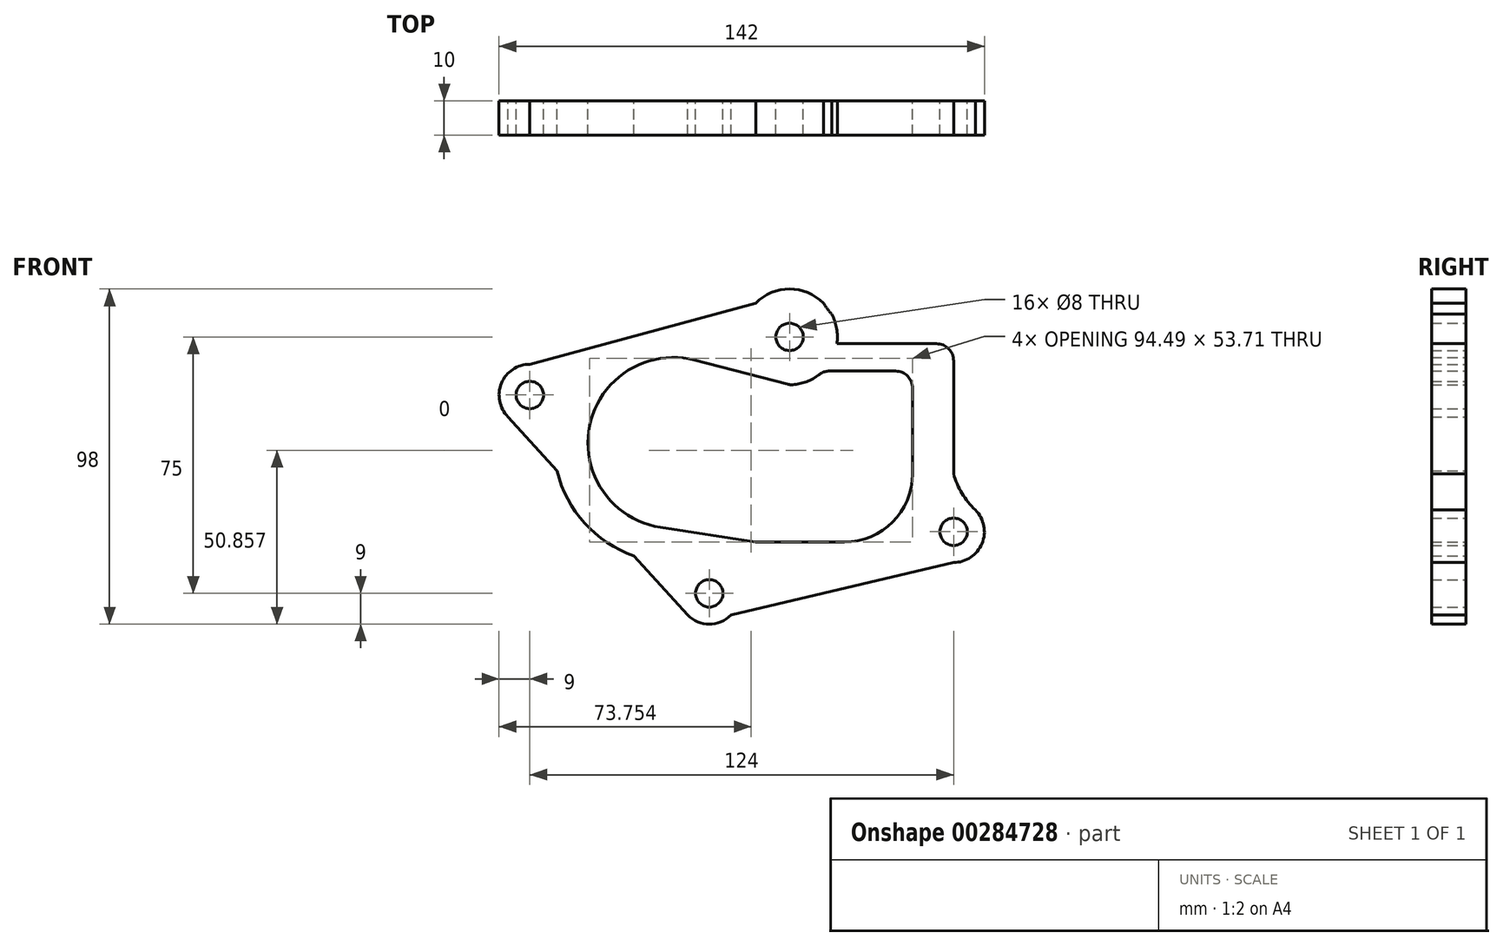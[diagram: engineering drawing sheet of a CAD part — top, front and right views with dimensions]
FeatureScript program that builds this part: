
annotation { "Feature Type Name" : "Feature", "Feature Type Description" : "" }
export const myFeature = defineFeature(function(context is Context, id is Id, definition is map)
    precondition{}
    {
        {
            var Q0;
            Q0=qCreatedBy(makeId("Front.planeOp"),FACE);
            var sketch = newSketch(context, id + "F0", { "sketchPlane" : qUnion([Q0])});
            skCircle(sketch, "E0", {"center": v(0, 0) * mm, "radius": 25 * mm});
            skLineSegment(sketch, "E1", {"start": v(0, 0) * mm, "end": v(70, 0) * mm});
            skPoint(sketch, "E2", {"position": v(34, 31) * mm});
            skArc(sketch, "E3", {"start": v(34.89, 17.03) * mm, "mid": v(38.96, 17.9) * mm, "end": v(42.6, 19.95) * mm, "construction": true});
            skLineSegment(sketch, "E4", {"start": v(34, 31) * mm, "end": v(34, 17) * mm, "construction": true});
            skPoint(sketch, "E5", {"position": v(0, 25) * mm});
            skLineSegment(sketch, "E6", {"start": v(33.31, 17.18) * mm, "end": v(6.28, 24.2) * mm});
            skLineSegment(sketch, "E7", {"start": v(70, 0) * mm, "end": v(70, -9) * mm});
            skLineSegment(sketch, "E8", {"start": v(50, -29) * mm, "end": v(24, -29) * mm});
            skPoint(sketch, "E9.visualSharp", {"position": v(70, -29) * mm});
            skArc(sketch, "E9.filletArc", {"start": v(50, -29) * mm, "mid": v(64.14, -23.14) * mm, "end": v(70, -9) * mm});
            skPoint(sketch, "E10.visualSharp", {"position": v(34, 17) * mm});
            skArc(sketch, "E10.filletArc", {"start": v(33.31, 17.18) * mm, "mid": v(34.1, 17.04) * mm, "end": v(34.89, 17.03) * mm});
            skLineSegment(sketch, "E11", {"start": v(24, -29) * mm, "end": v(-3.81, -24.7) * mm});
            skPoint(sketch, "E12", {"position": v(25, 0) * mm});
            skCircle(sketch, "E13", {"center": v(0, 0) * mm, "radius": 35 * mm, "construction": true});
            skPoint(sketch, "E14", {"position": v(-42, 14) * mm});
            skPoint(sketch, "E15", {"position": v(10.5, -44) * mm});
            skPoint(sketch, "E16", {"position": v(82, -26) * mm});
            skLineSegment(sketch, "E17", {"start": v(65.66, 21) * mm, "end": v(43.8, 21) * mm});
            skArc(sketch, "E18", {"start": v(43.8, 21) * mm, "mid": v(39.7, 18.21) * mm, "end": v(34.89, 17.03) * mm});
            skCircle(sketch, "E19", {"center": v(-42, 14) * mm, "radius": 4 * mm});
            skCircle(sketch, "E20", {"center": v(10.5, -44) * mm, "radius": 4 * mm});
            skCircle(sketch, "E21", {"center": v(82, -26) * mm, "radius": 4 * mm});
            skCircle(sketch, "E22", {"center": v(34, 31) * mm, "radius": 4 * mm});
            skPoint(sketch, "E23", {"position": v(30, 18.04) * mm});
            skPoint(sketch, "E24", {"position": v(20.4, -28.44) * mm});
            skArc(sketch, "E25", {"start": v(30, 18.04) * mm, "mid": v(-34.28, 7.08) * mm, "end": v(20.4, -28.44) * mm});
            skPoint(sketch, "E26", {"position": v(20.21, 28.57) * mm});
            skArc(sketch, "E27", {"start": v(20.21, 28.57) * mm, "mid": v(38.28, 44.33) * mm, "end": v(43.8, 21) * mm});
            skLineSegment(sketch, "E28", {"start": v(68, 21) * mm, "end": v(82, 21) * mm});
            skLineSegment(sketch, "E29", {"start": v(82, 21) * mm, "end": v(82, 24) * mm});
            skLineSegment(sketch, "E30", {"start": v(77, 29) * mm, "end": v(47.86, 29) * mm});
            skCircle(sketch, "E31", {"center": v(82, -26) * mm, "radius": 9 * mm});
            skLineSegment(sketch, "E32", {"start": v(82, 21) * mm, "end": v(82, -17) * mm});
            skPoint(sketch, "E33", {"position": v(82, -35) * mm});
            skCircle(sketch, "E34", {"center": v(10.5, -44) * mm, "radius": 9 * mm});
            skLineSegment(sketch, "E35", {"start": v(82, -35) * mm, "end": v(10.5, -35) * mm});
            skCircle(sketch, "E36", {"center": v(-42, 14) * mm, "radius": 9 * mm});
            skPoint(sketch, "E37", {"position": v(-42, 23) * mm});
            skPoint(sketch, "E38", {"position": v(-24.5, 25) * mm});
            skArc(sketch, "E39", {"start": v(-42, 23) * mm, "mid": v(-33.02, 21.97) * mm, "end": v(-24.5, 25) * mm});
            skLineSegment(sketch, "E40", {"start": v(-42, 14) * mm, "end": v(-38, 14) * mm, "construction": true});
            skPoint(sketch, "E41", {"position": v(-42, 5) * mm});
            skPoint(sketch, "E42", {"position": v(-34.3, -7) * mm});
            skArc(sketch, "E43", {"start": v(-34.3, -7) * mm, "mid": v(-36.17, 0.27) * mm, "end": v(-42, 5) * mm});
            skPoint(sketch, "E44", {"position": v(25.5, -35) * mm});
            skPoint(sketch, "E45", {"position": v(19.5, -44) * mm});
            skArc(sketch, "E46", {"start": v(25.5, -35) * mm, "mid": v(20.75, -38.33) * mm, "end": v(19.5, -44) * mm});
            skPoint(sketch, "E47", {"position": v(0, -35) * mm});
            skPoint(sketch, "E48", {"position": v(1.5, -44) * mm});
            skArc(sketch, "E49", {"start": v(1.5, -44) * mm, "mid": v(1.64, -39.35) * mm, "end": v(0, -35) * mm});
            skLineSegment(sketch, "E50", {"start": v(70, 0) * mm, "end": v(70, 16) * mm});
            skLineSegment(sketch, "E51", {"start": v(65, 21) * mm, "end": v(45.66, 21) * mm});
            skPoint(sketch, "E52.visualSharp", {"position": v(70, 21) * mm});
            skArc(sketch, "E52.filletArc", {"start": v(70, 16) * mm, "mid": v(68.54, 19.54) * mm, "end": v(65, 21) * mm});
            skPoint(sketch, "E53", {"position": v(0, 35) * mm});
            skPoint(sketch, "E54", {"position": v(34, 45) * mm});
            skLineSegment(sketch, "E55", {"start": v(34, 31) * mm, "end": v(24.1, 40.9) * mm, "construction": true});
            skLineSegment(sketch, "E56", {"start": v(34, 31) * mm, "end": v(34, 45) * mm});
            skArc(sketch, "E57", {"start": v(0, 35) * mm, "mid": v(12.69, 35.34) * mm, "end": v(24.1, 40.9) * mm});
            skPoint(sketch, "E58.visualSharp", {"position": v(82, 29) * mm});
            skArc(sketch, "E58.filletArc", {"start": v(82, 24) * mm, "mid": v(80.54, 27.54) * mm, "end": v(77, 29) * mm});
            skLineSegment(sketch, "E59", {"start": v(34, 31) * mm, "end": v(43.9, 40.9) * mm, "construction": true});
            skLineSegment(sketch, "E60", {"start": v(47.86, 29) * mm, "end": v(59.86, 29) * mm});
            skArc(sketch, "E61", {"start": v(43.9, 40.9) * mm, "mid": v(50.78, 33.48) * mm, "end": v(59.86, 29) * mm});
            skLineSegment(sketch, "E62", {"start": v(10.5, -44) * mm, "end": v(4.14, -50.36) * mm});
            skLineSegment(sketch, "E63", {"start": v(10.5, -44) * mm, "end": v(10.5, -47) * mm, "construction": true});
            skLineSegment(sketch, "E64", {"start": v(-42, 14) * mm, "end": v(-51, 14) * mm});
            skLineSegment(sketch, "E65", {"start": v(-42, 14) * mm, "end": v(-48.36, 7.64) * mm});
            skLineSegment(sketch, "E66", {"start": v(-48.36, 7.64) * mm, "end": v(4.14, -50.36) * mm});
            skPoint(sketch, "E67", {"position": v(16.86, -50.36) * mm});
            skLineSegment(sketch, "E68", {"start": v(10.5, -44) * mm, "end": v(16.86, -50.36) * mm});
            skLineSegment(sketch, "E69", {"start": v(16.86, -50.36) * mm, "end": v(82, -35) * mm});
            skLineSegment(sketch, "E70", {"start": v(82, -26) * mm, "end": v(88.36, -19.64) * mm});
            skLineSegment(sketch, "E71", {"start": v(82, -26) * mm, "end": v(85, -26) * mm});
            skPoint(sketch, "E72", {"position": v(82, -9) * mm});
            skArc(sketch, "E73", {"start": v(82, -9) * mm, "mid": v(84.45, -14.75) * mm, "end": v(88.36, -19.64) * mm});
            skLineSegment(sketch, "E74", {"start": v(-42, 23) * mm, "end": v(24.1, 40.9) * mm});
            skArc(sketch, "E75.filletArc", {"start": v(45.66, 21) * mm, "mid": v(44.04, 20.73) * mm, "end": v(42.6, 19.95) * mm});
            skSolve(sketch);
        }
        {
            var Q0;
            {var subQ13=sQuery(id+"F0.wireOp",EDGE,"E0");var subQ19=sQuery(id+"F0.wireOp",EDGE,"E6");var subQ20=makeQuery(id+"F0.imprint","INTERSECT",VERTEX,{"derivedFrom":[subQ13,subQ19]});Q0=makeQuery(id+"F0.imprint","IMPRINT",FACE,{"disambiguationData":[TD([[makeQuery(id+"F0.imprint","IMPRINT",EDGE,{"disambiguationData":[TD([[subQ20,-1.0]])],"derivedFrom":subQ13}),-1.0]])]});}
            var Q1;
            {var subQ0=sQuery(id+"F0.wireOp",EDGE,"E39");var subQ1=sQuery(id+"F0.wireOp",EDGE,"E25");var subQ2=makeQuery(id+"F0.imprint","INTERSECT",VERTEX,{"derivedFrom":[subQ1,subQ0]});Q1=makeQuery(id+"F0.imprint","IMPRINT",FACE,{"disambiguationData":[TD([[makeQuery(id+"F0.imprint","IMPRINT",EDGE,{"disambiguationData":[TD([[subQ2,-1.0]])],"derivedFrom":subQ1}),-1.0]])]});}
            var Q2;
            {var subQ0=sQuery(id+"F0.wireOp",EDGE,"E43");var subQ3=sQuery(id+"F0.wireOp",EDGE,"E25");var subQ7=makeQuery(id+"F0.imprint","INTERSECT",VERTEX,{"disambiguationData":[OD(0.0)],"derivedFrom":[subQ3,subQ0]});Q2=makeQuery(id+"F0.imprint","IMPRINT",FACE,{"disambiguationData":[TD([[makeQuery(id+"F0.imprint","IMPRINT",EDGE,{"disambiguationData":[TD([[subQ7,1.0]])],"derivedFrom":subQ3}),-1.0]])]});}
            var Q3;
            {var subQ0=sQuery(id+"F0.wireOp",EDGE,"E39");var subQ1=sQuery(id+"F0.wireOp",EDGE,"E25");var subQ2=makeQuery(id+"F0.imprint","INTERSECT",VERTEX,{"derivedFrom":[subQ1,subQ0]});Q3=makeQuery(id+"F0.imprint","IMPRINT",FACE,{"disambiguationData":[TD([[makeQuery(id+"F0.imprint","IMPRINT",EDGE,{"disambiguationData":[TD([[subQ2,1.0]])],"derivedFrom":subQ1}),-1.0]])]});}
            var Q4;
            {var subQ3=sQuery(id+"F0.wireOp",EDGE,"E64");var subQ5=sQuery(id+"F0.wireOp",EDGE,"E19");var subQ6=makeQuery(id+"F0.imprint","INTERSECT",VERTEX,{"derivedFrom":[subQ5,subQ3]});Q4=makeQuery(id+"F0.imprint","IMPRINT",FACE,{"disambiguationData":[TD([[makeQuery(id+"F0.imprint","IMPRINT",EDGE,{"disambiguationData":[TD([[subQ6,1.0]])],"derivedFrom":subQ5}),-1.0]])]});}
            var Q5;
            {var subQ0=sQuery(id+"F0.wireOp",EDGE,"E64");var subQ1=sQuery(id+"F0.wireOp",EDGE,"E19");var subQ2=makeQuery(id+"F0.imprint","INTERSECT",VERTEX,{"derivedFrom":[subQ1,subQ0]});Q5=makeQuery(id+"F0.imprint","IMPRINT",FACE,{"disambiguationData":[TD([[makeQuery(id+"F0.imprint","IMPRINT",EDGE,{"disambiguationData":[TD([[subQ2,-1.0]])],"derivedFrom":subQ1}),-1.0]])]});}
            var Q6;
            {var subQ0=sQuery(id+"F0.wireOp",EDGE,"E39");var subQ1=sQuery(id+"F0.wireOp",EDGE,"E36");var subQ3=makeQuery(id+"F0.imprint","INTERSECT",VERTEX,{"derivedFrom":[subQ1,subQ0]});Q6=makeQuery(id+"F0.imprint","IMPRINT",FACE,{"disambiguationData":[TD([[makeQuery(id+"F0.imprint","IMPRINT",EDGE,{"disambiguationData":[TD([[subQ3,-1.0]])],"derivedFrom":subQ1}),1.0]])]});}
            var Q7;
            {var subQ0=sQuery(id+"F0.wireOp",EDGE,"E66");var subQ1=sQuery(id+"F0.wireOp",EDGE,"E25");var subQ2=makeQuery(id+"F0.imprint","INTERSECT",VERTEX,{"disambiguationData":[OD(0.0)],"derivedFrom":[subQ1,subQ0]});Q7=makeQuery(id+"F0.imprint","IMPRINT",FACE,{"disambiguationData":[TD([[makeQuery(id+"F0.imprint","IMPRINT",EDGE,{"disambiguationData":[TD([[subQ2,-1.0]])],"derivedFrom":subQ1}),1.0]])]});}
            var Q8;
            {var subQ0=sQuery(id+"F0.wireOp",EDGE,"E69");Q8=makeQuery(id+"F0.imprint","IMPRINT",FACE,{"disambiguationData":[TD([[makeQuery(id+"F0.imprint","IMPRINT",EDGE,{"derivedFrom":subQ0}),1.0]])]});}
            var Q9;
            {var subQ12=sQuery(id+"F0.wireOp",EDGE,"E62");var subQ13=sQuery(id+"F0.wireOp",EDGE,"E20");var subQ14=makeQuery(id+"F0.imprint","INTERSECT",VERTEX,{"derivedFrom":[subQ13,subQ12]});Q9=makeQuery(id+"F0.imprint","IMPRINT",FACE,{"disambiguationData":[TD([[makeQuery(id+"F0.imprint","IMPRINT",EDGE,{"disambiguationData":[TD([[subQ14,1.0]])],"derivedFrom":subQ13}),-1.0]])]});}
            var Q10;
            {var subQ0=sQuery(id+"F0.wireOp",EDGE,"E35");var subQ1=sQuery(id+"F0.wireOp",EDGE,"E34");var subQ2=makeQuery(id+"F0.imprint","INTERSECT",VERTEX,{"derivedFrom":[subQ1,subQ0]});Q10=makeQuery(id+"F0.imprint","IMPRINT",FACE,{"disambiguationData":[TD([[makeQuery(id+"F0.imprint","IMPRINT",EDGE,{"disambiguationData":[TD([[subQ2,1.0]])],"derivedFrom":subQ1}),-1.0]])]});}
            var Q11;
            {var subQ0=sQuery(id+"F0.wireOp",EDGE,"E62");var subQ1=sQuery(id+"F0.wireOp",EDGE,"E20");var subQ2=makeQuery(id+"F0.imprint","INTERSECT",VERTEX,{"derivedFrom":[subQ1,subQ0]});Q11=makeQuery(id+"F0.imprint","IMPRINT",FACE,{"disambiguationData":[TD([[makeQuery(id+"F0.imprint","IMPRINT",EDGE,{"disambiguationData":[TD([[subQ2,-1.0]])],"derivedFrom":subQ1}),-1.0]])]});}
            var Q12;
            {var subQ0=sQuery(id+"F0.wireOp",EDGE,"E49");var subQ1=sQuery(id+"F0.wireOp",EDGE,"E25");var subQ2=makeQuery(id+"F0.imprint","INTERSECT",VERTEX,{"derivedFrom":[subQ1,subQ0]});Q12=makeQuery(id+"F0.imprint","IMPRINT",FACE,{"disambiguationData":[TD([[makeQuery(id+"F0.imprint","IMPRINT",EDGE,{"disambiguationData":[TD([[subQ2,1.0]])],"derivedFrom":subQ1}),-1.0]])]});}
            var Q13;
            {var subQ0=sQuery(id+"F0.wireOp",EDGE,"E49");var subQ1=sQuery(id+"F0.wireOp",EDGE,"E34");var subQ2=makeQuery(id+"F0.imprint","INTERSECT",VERTEX,{"disambiguationData":[OD(0.0)],"derivedFrom":[subQ1,subQ0]});Q13=makeQuery(id+"F0.imprint","IMPRINT",FACE,{"disambiguationData":[TD([[makeQuery(id+"F0.imprint","IMPRINT",EDGE,{"disambiguationData":[TD([[subQ2,1.0]])],"derivedFrom":subQ1}),1.0]])]});}
            var Q14;
            Q14=makeQuery(id+"F0.imprint","IMPRINT",FACE,{"disambiguationData":[TD([[makeQuery(id+"F0.imprint","IMPRINT",EDGE,{"derivedFrom":sQuery(id+"F0.wireOp",EDGE,"E7")}),1.0]])]});
            var Q15;
            {var subQ12=sQuery(id+"F0.wireOp",EDGE,"E10.filletArc");Q15=makeQuery(id+"F0.imprint","IMPRINT",FACE,{"disambiguationData":[TD([[makeQuery(id+"F0.imprint","IMPRINT",EDGE,{"derivedFrom":subQ12}),1.0]])]});}
            var Q16;
            {var subQ0=sQuery(id+"F0.wireOp",EDGE,"E27");var subQ1=sQuery(id+"F0.wireOp",EDGE,"E25");var subQ2=makeQuery(id+"F0.imprint","INTERSECT",VERTEX,{"derivedFrom":[subQ1,subQ0]});Q16=makeQuery(id+"F0.imprint","IMPRINT",FACE,{"disambiguationData":[TD([[makeQuery(id+"F0.imprint","IMPRINT",EDGE,{"disambiguationData":[TD([[subQ2,-1.0]])],"derivedFrom":subQ1}),-1.0]])]});}
            var Q17;
            {var subQ0=sQuery(id+"F0.wireOp",EDGE,"E74");var subQ1=sQuery(id+"F0.wireOp",EDGE,"E25");var subQ2=makeQuery(id+"F0.imprint","INTERSECT",VERTEX,{"disambiguationData":[OD(0.0)],"derivedFrom":[subQ1,subQ0]});Q17=makeQuery(id+"F0.imprint","IMPRINT",FACE,{"disambiguationData":[TD([[makeQuery(id+"F0.imprint","IMPRINT",EDGE,{"disambiguationData":[TD([[subQ2,1.0]])],"derivedFrom":subQ1}),-1.0]])]});}
            var Q18;
            {var subQ0=sQuery(id+"F0.wireOp",EDGE,"E57");var subQ1=sQuery(id+"F0.wireOp",EDGE,"E25");var subQ2=makeQuery(id+"F0.imprint","INTERSECT",VERTEX,{"disambiguationData":[OD(0.0)],"derivedFrom":[subQ1,subQ0]});Q18=makeQuery(id+"F0.imprint","IMPRINT",FACE,{"disambiguationData":[TD([[makeQuery(id+"F0.imprint","IMPRINT",EDGE,{"disambiguationData":[TD([[subQ2,-1.0]])],"derivedFrom":subQ1}),1.0]])]});}
            var Q19;
            {var subQ0=sQuery(id+"F0.wireOp",EDGE,"E60");Q19=makeQuery(id+"F0.imprint","IMPRINT",FACE,{"disambiguationData":[TD([[makeQuery(id+"F0.imprint","IMPRINT",EDGE,{"derivedFrom":subQ0}),1.0]])]});}
            var Q20;
            Q20=makeQuery(id+"F0.imprint","IMPRINT",FACE,{"disambiguationData":[TD([[makeQuery(id+"F0.imprint","IMPRINT",EDGE,{"derivedFrom":sQuery(id+"F0.wireOp",EDGE,"E21")}),-1.0]])]});
            var Q21;
            {var subQ0=sQuery(id+"F0.wireOp",EDGE,"E32");var subQ1=sQuery(id+"F0.wireOp",EDGE,"E31");var subQ2=makeQuery(id+"F0.imprint","INTERSECT",VERTEX,{"derivedFrom":[subQ1,subQ0]});Q21=makeQuery(id+"F0.imprint","IMPRINT",FACE,{"disambiguationData":[TD([[makeQuery(id+"F0.imprint","IMPRINT",EDGE,{"disambiguationData":[TD([[subQ2,1.0]])],"derivedFrom":subQ1}),-1.0]])]});}
            var Q22;
            {var subQ0=sQuery(id+"F0.wireOp",EDGE,"E74");var subQ1=sQuery(id+"F0.wireOp",EDGE,"E25");var subQ2=makeQuery(id+"F0.imprint","INTERSECT",VERTEX,{"disambiguationData":[OD(0.0)],"derivedFrom":[subQ1,subQ0]});Q22=makeQuery(id+"F0.imprint","IMPRINT",FACE,{"disambiguationData":[TD([[makeQuery(id+"F0.imprint","IMPRINT",EDGE,{"disambiguationData":[TD([[subQ2,1.0]])],"derivedFrom":subQ1}),1.0]])]});}
            var Q23;
            {var subQ0=sQuery(id+"F0.wireOp",EDGE,"E57");var subQ1=sQuery(id+"F0.wireOp",EDGE,"E25");var subQ2=makeQuery(id+"F0.imprint","INTERSECT",VERTEX,{"disambiguationData":[OD(0.0)],"derivedFrom":[subQ1,subQ0]});Q23=makeQuery(id+"F0.imprint","IMPRINT",FACE,{"disambiguationData":[TD([[makeQuery(id+"F0.imprint","IMPRINT",EDGE,{"disambiguationData":[TD([[subQ2,1.0]])],"derivedFrom":subQ1}),1.0]])]});}
            var Q24;
            {var subQ0=sQuery(id+"F0.wireOp",EDGE,"E43");var subQ1=sQuery(id+"F0.wireOp",EDGE,"E25");var subQ2=makeQuery(id+"F0.imprint","INTERSECT",VERTEX,{"disambiguationData":[OD(0.0)],"derivedFrom":[subQ1,subQ0]});Q24=makeQuery(id+"F0.imprint","IMPRINT",FACE,{"disambiguationData":[TD([[makeQuery(id+"F0.imprint","IMPRINT",EDGE,{"disambiguationData":[TD([[subQ2,1.0]])],"derivedFrom":subQ1}),1.0]])]});}
            var Q25;
            {var subQ0=sQuery(id+"F0.wireOp",EDGE,"E46");var subQ1=sQuery(id+"F0.wireOp",EDGE,"E34");var subQ2=makeQuery(id+"F0.imprint","INTERSECT",VERTEX,{"disambiguationData":[OD(0.0)],"derivedFrom":[subQ1,subQ0]});Q25=makeQuery(id+"F0.imprint","IMPRINT",FACE,{"disambiguationData":[TD([[makeQuery(id+"F0.imprint","IMPRINT",EDGE,{"disambiguationData":[TD([[subQ2,-1.0]])],"derivedFrom":subQ1}),1.0]])]});}
            var Q26;
            {var subQ3=sQuery(id+"F0.wireOp",EDGE,"E75.filletArc");Q26=makeQuery(id+"F0.imprint","IMPRINT",FACE,{"disambiguationData":[TD([[makeQuery(id+"F0.imprint","IMPRINT",EDGE,{"derivedFrom":subQ3}),-1.0]])]});}
            extrude(context, id + "F1", {"entities" : qUnion([Q0, Q1, Q2, Q3, Q4, Q5, Q6, Q7, Q8, Q9, Q10, Q11, Q12, Q13, Q14, Q15, Q16, Q17, Q18, Q19, Q20, Q21, Q22, Q23, Q24, Q25, Q26]), "depth" : 10 * mm});
        }
    });
